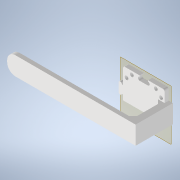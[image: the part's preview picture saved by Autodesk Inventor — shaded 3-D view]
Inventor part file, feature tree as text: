
AUTODESK INVENTOR PART (.ipt)
format: ipt  version: 2022 (Build 260153000, 153)  size: 293,888 bytes
history: native  units: mm
features: extrude x5, sketch x5, projected_geometry x5, chamfer x2, other x2, plane x1, fillet x1, reference x1
ambient origin geometry x8: Origin, YZ Plane, XZ Plane, XY Plane, X Axis, Y Axis, Z Axis, Center Point
bodies: Volumenkörper1 (feature_tree)
feature tree (22):
  plane  "Arbeitsebene1"
  extrude  "Extrusion1"  Depth=5.0mm
  chamfer  "Fase1"  Distance=5.0mm
  extrude  "Extrusion2"  Depth=8.0mm
  extrude  "Extrusion3"  Depth=5.0mm TaperAngle=0.0deg
  chamfer  "Fase2"  Distance=10.0mm Angle=45.0deg
  extrude  "Extrusion5"  Depth=10.0mm
  fillet  "Rundung1"  Radius=100.0mm
  extrude  "Extrusion6"  Depth=7.0mm
  sketch  "Skizze1"  dims[d0=5.0mm d2=6.0mm]
  reference  "Referenz1"
  sketch  "Skizze2"  dims[d3=6.0mm d4=5.0mm d5=0.0mm]
  sketch  "Skizze3"  dims[d6=1.0mm d7=2.0mm d8=45.0deg d9=8.0mm]
  projected_geometry  "Projizierte Kontur1"
  projected_geometry  "Projizierte Kontur2"
  sketch  "Skizze5"  dims[d10=45.0mm d11=0.0mm d13=5.0mm d14=0.0mm d15=10.0mm d16=2.0mm d17=45.0deg]
  projected_geometry  "Projizierte Kontur4"
  sketch  "Skizze6"  dims[d21=10.0mm d22=0.0mm d23=10.0mm d24=100.0mm d25=7.0mm d26=5.0mm d27=0.0mm d28=2.0mm]
  projected_geometry  "Projizierte Kontur5"
  projected_geometry  "Projizierte Kontur6"
  other  "Baugruppe1"
  other  "10_Base_puzzle_v3:1"
